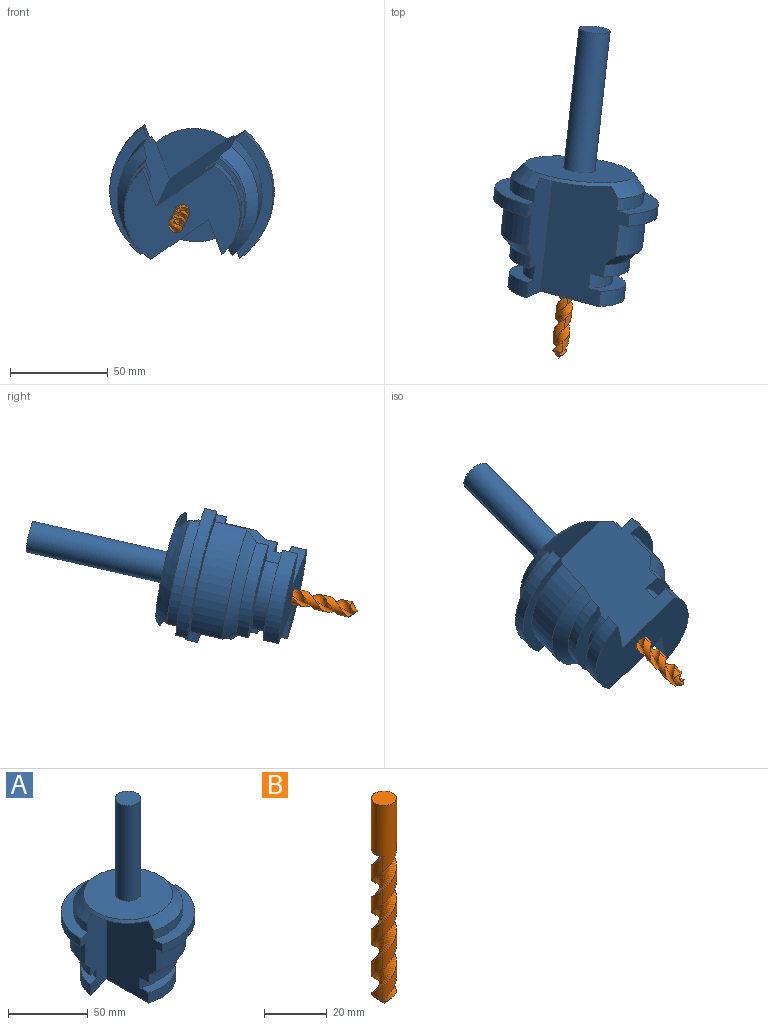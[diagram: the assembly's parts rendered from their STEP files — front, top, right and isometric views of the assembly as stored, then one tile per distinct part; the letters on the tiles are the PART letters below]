
ASSEMBLY  parts=2 mates=1
PART A: 36 faces, bbox 84.1x84.1x138.6 mm
  f0: cylinder r=29.86mm len=40.48mm, axis (0,0,1), area 435mm2, adj f2,f22,f31,f34
  f1: cylinder r=29.86mm len=39.67mm, axis (0,0,1), area 426.9mm2, adj f2,f23,f32,f35
  f2: plane 59.71x59.29mm, normal (0,0,-1), area 1717.3mm2, adj f0,f1,f24,f31,f32,f34,f35
  f3: cone r=34.27mm half-angle=40.9deg, axis (0,0,-1), area 1239.3mm2, adj f4,f5,f28,f29,f31,f32,f33,f34
  f4: cylinder r=34.27mm len=45.02mm, axis (0,0,1), area 408.5mm2, adj f3,f6,f31,f34
  f5: cylinder r=34.27mm len=44.22mm, axis (0,0,1), area 401.8mm2, adj f3,f7,f32,f35
  f6: plane 52.76x41.93mm, normal (0,0,1), area 535.1mm2, adj f4,f8,f30,f31,f34
  f7: plane 51.97x41.75mm, normal (0,0,1), area 527.1mm2, adj f5,f9,f32,f35
  f8: cylinder r=41.93mm len=52.76mm, axis (0,0,1), area 486.1mm2, adj f6,f10,f30,f34
  f9: cylinder r=41.93mm len=51.97mm, axis (0,0,1), area 479.7mm2, adj f7,f11,f32,f35
  f10: plane 52.76x41.93mm, normal (0,0,-1), area 398.8mm2, adj f8,f12,f30,f31,f34
  f11: plane 51.97x41.75mm, normal (0,0,-1), area 393mm2, adj f9,f13,f32,f35
  f12: cylinder r=36.37mm len=47.17mm, axis (0,0,1), area 1136.1mm2, adj f10,f14,f31,f34
  f13: cylinder r=36.37mm len=46.37mm, axis (0,0,1), area 1118.5mm2, adj f11,f15,f32,f35
  f14: cone r=30.62mm half-angle=44.1deg, axis (0,0,1), area 506.6mm2, adj f12,f16,f31,f34
  f15: cone r=30.62mm half-angle=44.1deg, axis (0,0,1), area 498mm2, adj f13,f17,f32,f35
  f16: cylinder r=30.62mm len=41.28mm, axis (0,0,1), area 353.8mm2, adj f14,f18,f31,f34
  f17: cylinder r=30.62mm len=40.47mm, axis (0,0,1), area 347.3mm2, adj f15,f19,f32,f35
  f18: plane 41.28x27.39mm, normal (0,0,-1), area 374.3mm2, adj f16,f20,f31,f34
  f19: plane 40.47x27.2mm, normal (0,0,-1), area 366.4mm2, adj f17,f21,f32,f35
  f20: cylinder r=22.95mm len=33.09mm, axis (0,0,1), area 319.7mm2, adj f18,f22,f31,f34
  f21: cylinder r=22.95mm len=32.26mm, axis (0,0,1), area 311.7mm2, adj f19,f23,f32,f35
  f22: plane 40.48x26.39mm, normal (0,0,1), area 332mm2, adj f0,f20,f31,f34
  f23: plane 39.67x26.21mm, normal (0,0,1), area 324.9mm2, adj f1,f21,f32,f35
  f24: cylinder r=4mm len=45.54mm, axis (0,0,1), area 1144.5mm2, adj f2,f25
  f25: plane 8x8mm, normal (0,0,-1), area 50.3mm2, adj f24
  f26: plane 16x16mm, normal (0,0,1), area 201.1mm2, adj f27
  f27: cylinder r=8mm len=73.46mm, axis (0,0,1), area 3692.4mm2, adj f26,f28
  f28: plane 56.26x56.26mm, normal (0,0,1), area 2284.8mm2, adj f3,f27
  f29: plane 36.98x19.62mm, normal (0,0,-1), area 521.7mm2, adj f3,f31,f32
  f30: plane 6.33x0.17mm, normal (0,-1,0), area 1.1mm2, adj f6,f8,f10,f31
  f31: plane 63.35x31.92mm, normal (0.28,-0.96,0), area 1499.4mm2, adj f0,f2,f3,f4,f6,f10,f12,f14
  f32: plane 63.32x49.95mm, normal (-1,0,0), area 2558.6mm2, adj f1,f2,f3,f5,f7,f9,f11,f13
  f33: plane 36.56x18.83mm, normal (0,0,-1), area 495.3mm2, adj f3,f34,f35
  f34: plane 63.34x49.64mm, normal (1,0,0), area 2533.1mm2, adj f0,f2,f3,f4,f6,f8,f10,f12
  f35: plane 63.35x31.3mm, normal (-0.27,0.96,0), area 1446.1mm2, adj f1,f2,f3,f5,f7,f9,f11,f13
PART B: 14 faces, bbox 8.6x8.4x80.1 mm
  f0: cylinder r=4mm len=38.5mm, axis (0,0,-1), area 607.2mm2, adj f1,f3,f6,f7,f8,f9,f10,f11
  f1: cylinder r=4mm len=30.46mm, axis (0,0,-1), area 137.3mm2, adj f0,f2,f8,f12
  f2: cylinder r=4mm len=17.96mm, axis (0,0,-1), area 83.6mm2, adj f1,f8,f12,f13
  f3: cylinder r=4mm len=30.46mm, axis (0,0,-1), area 137.3mm2, adj f0,f4,f9,f11
  f4: cylinder r=4mm len=30.46mm, axis (0,0,-1), area 137.3mm2, adj f3,f5,f9,f11
  f5: cylinder r=4mm len=5.46mm, axis (0,0,-1), area 15mm2, adj f4,f9,f13
  f6: plane 8x8mm, normal (0,0,1), area 50.3mm2, adj f0
  f7: plane 6.28x3.18mm, normal (0,0,-1), area 11.8mm2, adj f0,f8,f9
  f8: bspline ~62.5x8.55mm, area 190.5mm2, adj f0,f1,f2,f7,f9,f13
  f9: bspline ~62.5x8.35mm, area 284.6mm2, adj f0,f3,f4,f5,f7,f8,f13
  f10: plane 6.28x3.18mm, normal (0,0,-1), area 11.8mm2, adj f0,f11,f12
  f11: bspline ~62.5x8.55mm, area 190.5mm2, adj f0,f3,f4,f10,f12,f13
  f12: bspline ~62.5x8.35mm, area 282.3mm2, adj f0,f1,f2,f10,f11,f13
  f13: bspline ~8x7.99mm, area 37.8mm2, adj f2,f5,f8,f9,f11,f12
PLACE A rot(axis=(-0.76,0.45,0.46),89.4deg) t=(31.4,-149.85,214.33)mm
PLACE B rot(axis=(-0.68,0.5,0.54),95.4deg) t=(21.12,-244.53,192.84)mm
MATE revolute A.f0 <-> B.f0  axis (-0.11,-0.97,-0.22) through (29.55,-166.94,210.45)mm
